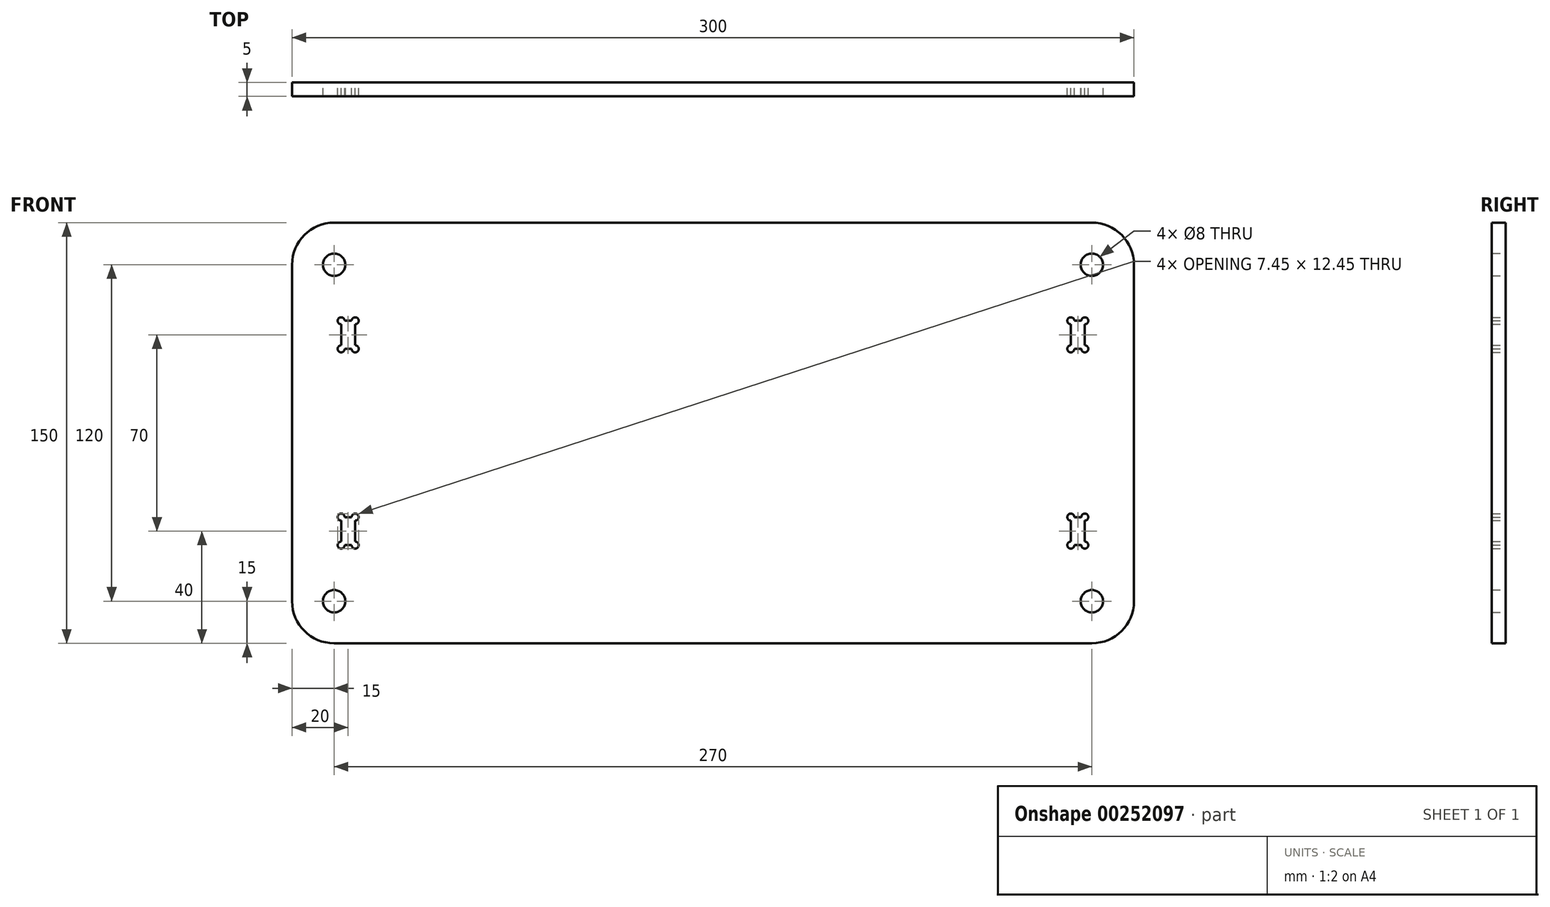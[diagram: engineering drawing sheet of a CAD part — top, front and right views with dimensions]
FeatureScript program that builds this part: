
annotation { "Feature Type Name" : "Feature", "Feature Type Description" : "" }
export const myFeature = defineFeature(function(context is Context, id is Id, definition is map)
    precondition{}
    {
        {
            var Q0;
            Q0=qCreatedBy(makeId("Front.planeOp"),FACE);
            var sketch = newSketch(context, id + "F0", { "sketchPlane" : qUnion([Q0])});
            skLineSegment(sketch, "E0.bottom", {"start": v(135, 75) * mm, "end": v(-135, 75) * mm});
            skLineSegment(sketch, "E0.top", {"start": v(135, -75) * mm, "end": v(-135, -75) * mm});
            skLineSegment(sketch, "E0.left", {"start": v(150, 60) * mm, "end": v(150, -60) * mm});
            skLineSegment(sketch, "E0.right", {"start": v(-150, 60) * mm, "end": v(-150, -60) * mm});
            skPoint(sketch, "E0.middle", {"position": v(0, 0) * mm});
            skLineSegment(sketch, "E1.bottom", {"start": v(-127.5, 30) * mm, "end": v(-132.5, 30) * mm});
            skLineSegment(sketch, "E1.top", {"start": v(-127.5, 40) * mm, "end": v(-132.5, 40) * mm});
            skLineSegment(sketch, "E1.left", {"start": v(-127.5, 30) * mm, "end": v(-127.5, 40) * mm});
            skLineSegment(sketch, "E1.right", {"start": v(-132.5, 30) * mm, "end": v(-132.5, 40) * mm});
            skPoint(sketch, "E1.middle", {"position": v(-130, 35) * mm});
            skCircle(sketch, "E2", {"center": v(-132.5, 40) * mm, "radius": 1.25 * mm});
            skCircle(sketch, "E3", {"center": v(-127.5, 40) * mm, "radius": 1.25 * mm});
            skCircle(sketch, "E4", {"center": v(-132.5, 30) * mm, "radius": 1.25 * mm});
            skCircle(sketch, "E5", {"center": v(-127.5, 30) * mm, "radius": 1.25 * mm});
            skLineSegment(sketch, "E6.MirrorCS", {"start": v(127.5, 30) * mm, "end": v(127.5, 40) * mm});
            skPoint(sketch, "E7.MirrorP", {"position": v(130, 35) * mm});
            skLineSegment(sketch, "E8.MirrorCS", {"start": v(127.5, 30) * mm, "end": v(132.5, 30) * mm});
            skLineSegment(sketch, "E9.MirrorCS", {"start": v(127.5, 40) * mm, "end": v(132.5, 40) * mm});
            skLineSegment(sketch, "E10.MirrorCS", {"start": v(132.5, 30) * mm, "end": v(132.5, 40) * mm});
            skCircle(sketch, "E11.MirrorC", {"center": v(127.5, 30) * mm, "radius": 1.25 * mm});
            skCircle(sketch, "E12.MirrorC", {"center": v(132.5, 30) * mm, "radius": 1.25 * mm});
            skCircle(sketch, "E13.MirrorC", {"center": v(127.5, 40) * mm, "radius": 1.25 * mm});
            skCircle(sketch, "E14.MirrorC", {"center": v(132.5, 40) * mm, "radius": 1.25 * mm});
            skCircle(sketch, "E15.MirrorC", {"center": v(-132.5, -40) * mm, "radius": 1.25 * mm});
            skLineSegment(sketch, "E16.MirrorCS", {"start": v(-127.5, -30) * mm, "end": v(-127.5, -40) * mm});
            skLineSegment(sketch, "E17.MirrorCS", {"start": v(-127.5, -40) * mm, "end": v(-132.5, -40) * mm});
            skPoint(sketch, "E18.MirrorP", {"position": v(-130, -35) * mm});
            skCircle(sketch, "E19.MirrorC", {"center": v(-127.5, -30) * mm, "radius": 1.25 * mm});
            skCircle(sketch, "E20.MirrorC", {"center": v(-132.5, -30) * mm, "radius": 1.25 * mm});
            skCircle(sketch, "E21.MirrorC", {"center": v(-127.5, -40) * mm, "radius": 1.25 * mm});
            skLineSegment(sketch, "E22.MirrorCS", {"start": v(-132.5, -30) * mm, "end": v(-132.5, -40) * mm});
            skLineSegment(sketch, "E23.MirrorCS", {"start": v(-127.5, -30) * mm, "end": v(-132.5, -30) * mm});
            skCircle(sketch, "E24.MirrorC", {"center": v(127.5, -40) * mm, "radius": 1.25 * mm});
            skPoint(sketch, "E25.MirrorP", {"position": v(130, -35) * mm});
            skCircle(sketch, "E26.MirrorC", {"center": v(132.5, -30) * mm, "radius": 1.25 * mm});
            skLineSegment(sketch, "E27.MirrorCS", {"start": v(132.5, -30) * mm, "end": v(132.5, -40) * mm});
            skLineSegment(sketch, "E28.MirrorCS", {"start": v(127.5, -30) * mm, "end": v(127.5, -40) * mm});
            skCircle(sketch, "E29.MirrorC", {"center": v(132.5, -40) * mm, "radius": 1.25 * mm});
            skLineSegment(sketch, "E30.MirrorCS", {"start": v(127.5, -40) * mm, "end": v(132.5, -40) * mm});
            skLineSegment(sketch, "E31.MirrorCS", {"start": v(127.5, -30) * mm, "end": v(132.5, -30) * mm});
            skCircle(sketch, "E32.MirrorC", {"center": v(127.5, -30) * mm, "radius": 1.25 * mm});
            skPoint(sketch, "E33.visualSharp", {"position": v(-150, 75) * mm});
            skArc(sketch, "E33.filletArc", {"start": v(-135, 75) * mm, "mid": v(-145.6, 70.6) * mm, "end": v(-150, 60) * mm});
            skPoint(sketch, "E34.visualSharp", {"position": v(-150, -75) * mm});
            skArc(sketch, "E34.filletArc", {"start": v(-150, -60) * mm, "mid": v(-145.6, -70.6) * mm, "end": v(-135, -75) * mm});
            skPoint(sketch, "E35.visualSharp", {"position": v(150, -75) * mm});
            skArc(sketch, "E35.filletArc", {"start": v(135, -75) * mm, "mid": v(145.6, -70.6) * mm, "end": v(150, -60) * mm});
            skPoint(sketch, "E36.visualSharp", {"position": v(150, 75) * mm});
            skArc(sketch, "E36.filletArc", {"start": v(150, 60) * mm, "mid": v(145.6, 70.6) * mm, "end": v(135, 75) * mm});
            skCircle(sketch, "E37", {"center": v(-135, 60) * mm, "radius": 4 * mm});
            skCircle(sketch, "E38.MirrorC", {"center": v(135, 60) * mm, "radius": 4 * mm});
            skCircle(sketch, "E39.MirrorC", {"center": v(-135, -60) * mm, "radius": 4 * mm});
            skCircle(sketch, "E40.MirrorC", {"center": v(135, -60) * mm, "radius": 4 * mm});
            skSolve(sketch);
        }
        {
            var Q0;
            Q0=makeQuery(id+"F0.imprint","IMPRINT",FACE,{"disambiguationData":[TD([[makeQuery(id+"F0.imprint","IMPRINT",EDGE,{"derivedFrom":sQuery(id+"F0.wireOp",EDGE,"E0.bottom")}),1.0]])]});
            extrude(context, id + "F1", {"entities" : qUnion([Q0]), "endBound" : BoundingType.SYMMETRIC, "depth" : 5 * mm});
        }
    });
